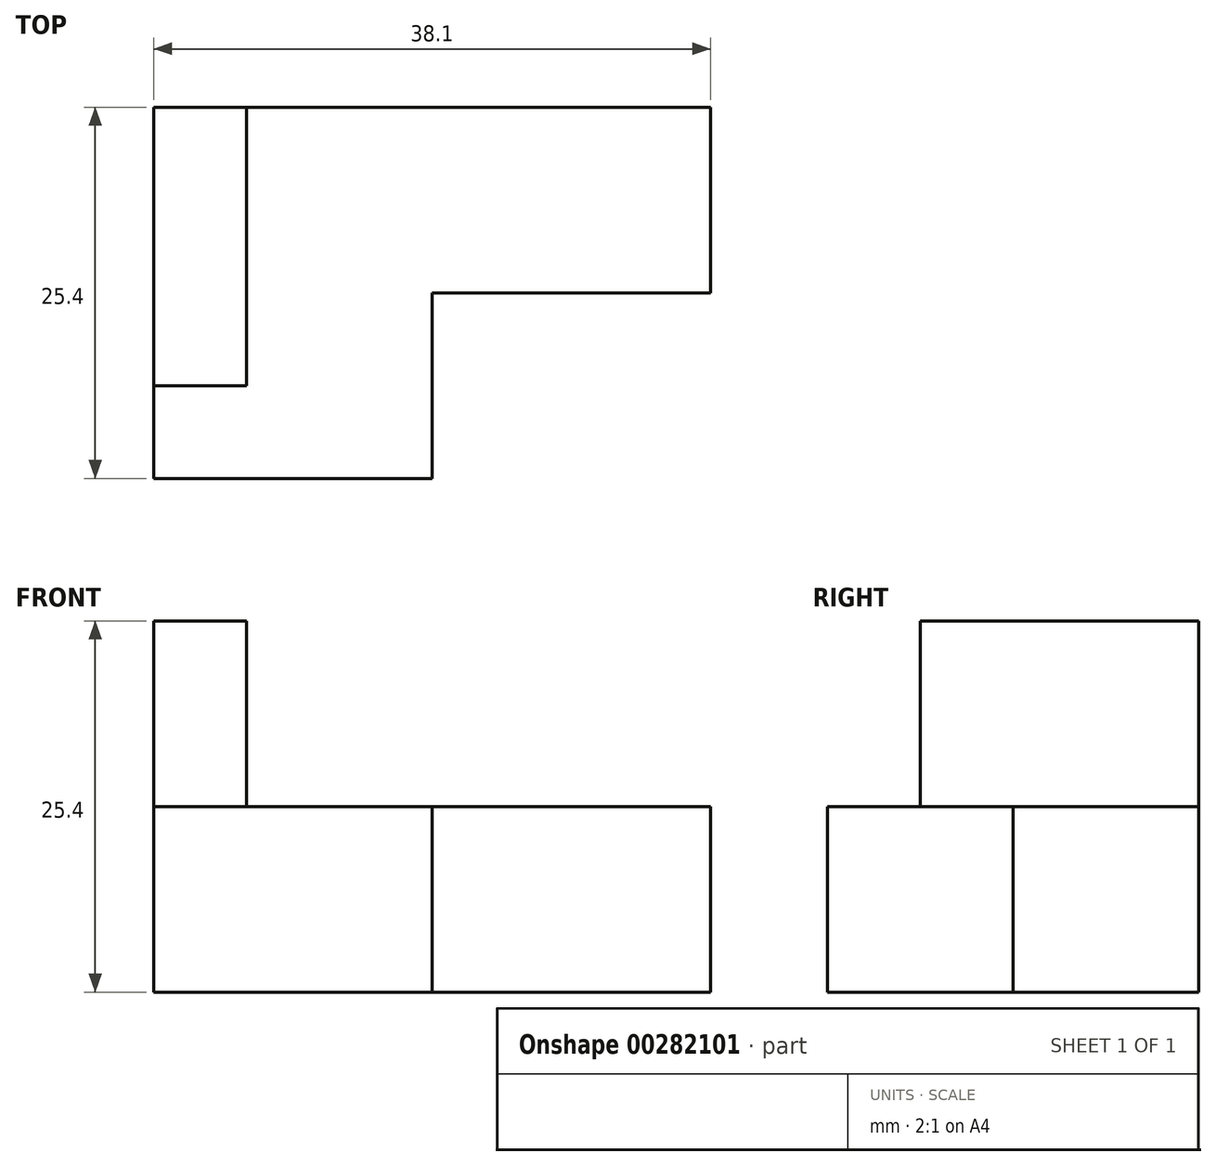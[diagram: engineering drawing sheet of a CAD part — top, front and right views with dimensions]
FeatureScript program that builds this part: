
annotation { "Feature Type Name" : "Feature", "Feature Type Description" : "" }
export const myFeature = defineFeature(function(context is Context, id is Id, definition is map)
    precondition{}
    {
        {
            var Q0;
            Q0=qCreatedBy(makeId("Front.planeOp"),FACE);
            var sketch = newSketch(context, id + "F0", { "sketchPlane" : qUnion([Q0])});
            skLineSegment(sketch, "E0", {"start": v(0, 0) * mm, "end": v(0, 12.7) * mm});
            skLineSegment(sketch, "E1", {"start": v(0, 12.7) * mm, "end": v(19.05, 12.7) * mm});
            skLineSegment(sketch, "E2", {"start": v(19.05, 12.7) * mm, "end": v(19.05, 0) * mm});
            skLineSegment(sketch, "E3", {"start": v(19.05, 0) * mm, "end": v(0, 0) * mm});
            skSolve(sketch);
        }
        {
            var Q0;
            Q0 = qSketchRegion(id + "F0", true);
            extrude(context, id + "F1", {"entities" : qUnion([Q0]), "depth" : 25.4 * mm});
        }
        {
            var Q0;
            Q0=makeQuery(id+"F1.opExtrude","SWEPT_FACE",FACE,{"disambiguationData":[OSD([sQuery(id+"F0.wireOp",EDGE,"E2")])]});
            var sketch = newSketch(context, id + "F2", { "sketchPlane" : qUnion([Q0])});
            skLineSegment(sketch, "E4", {"start": v(0, 0) * mm, "end": v(0, 12.7) * mm});
            skLineSegment(sketch, "E5", {"start": v(0, 12.7) * mm, "end": v(-12.7, 12.7) * mm});
            skLineSegment(sketch, "E6", {"start": v(-12.7, 12.7) * mm, "end": v(-12.7, 0) * mm});
            skLineSegment(sketch, "E7", {"start": v(-12.7, 0) * mm, "end": v(0, 0) * mm});
            skSolve(sketch);
        }
        {
            var Q0;
            Q0 = qSketchRegion(id + "F2", true);
            extrude(context, id + "F3", {"entities" : qUnion([Q0]), "operationType" : NewBodyOperationType.ADD, "depth" : 19.05 * mm});
        }
        {
            var Q0;
            Q0=makeQuery(id+"F3.boolean.opBoolean","MERGE",FACE,{"derivedFrom":[makeQuery(id+"F1.opExtrude","SWEPT_FACE",FACE,{"disambiguationData":[OSD([sQuery(id+"F0.wireOp",EDGE,"E1")])]}),makeQuery(id+"F3.opExtrude","SWEPT_FACE",FACE,{"disambiguationData":[OSD([sQuery(id+"F2.wireOp",EDGE,"E5")])]})]});
            var sketch = newSketch(context, id + "F4", { "sketchPlane" : qUnion([Q0])});
            skLineSegment(sketch, "E8", {"start": v(0, 0) * mm, "end": v(6.35, 0) * mm});
            skLineSegment(sketch, "E9", {"start": v(6.35, 0) * mm, "end": v(6.35, -19.05) * mm});
            skLineSegment(sketch, "E10", {"start": v(6.35, -19.05) * mm, "end": v(0, -19.05) * mm});
            skLineSegment(sketch, "E11", {"start": v(0, -19.05) * mm, "end": v(0, 0) * mm});
            skSolve(sketch);
        }
        {
            var Q0;
            Q0 = qSketchRegion(id + "F4", true);
            extrude(context, id + "F5", {"entities" : qUnion([Q0]), "operationType" : NewBodyOperationType.ADD, "depth" : 12.7 * mm});
        }
    });
